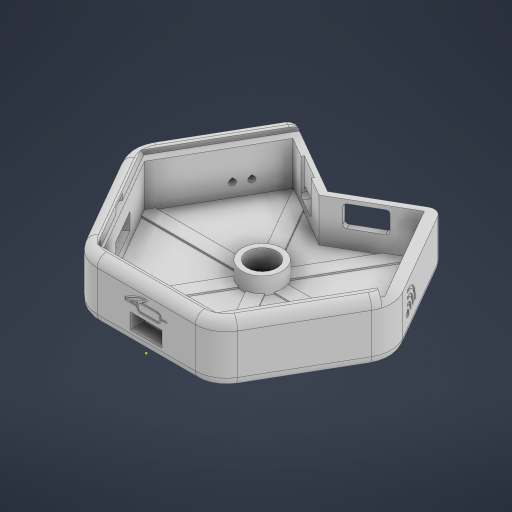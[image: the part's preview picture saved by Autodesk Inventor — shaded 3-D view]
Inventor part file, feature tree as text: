
AUTODESK INVENTOR PART (.ipt)
format: ipt  version: 2023 (Build 270158000, 158)  size: 1,028,096 bytes
history: native  units: in
note: dims shown in document units (in); Inventor stores cm internally (conversion verified against a paired STEP export)
features: extrude x21, sketch x15, move_body x9, direct_edit x6, fillet x5, draft x3, chamfer x1, other x1
ambient origin geometry x8: Origin, YZ Plane, XZ Plane, XY Plane, X Axis, Y Axis, Z Axis, Center Point
bodies: Solid1 (feature_tree)
feature tree (61):
  sketch  "Sketch1"  dims[d7=0.1772in d9=0.1772in d10=60.0deg d11=0.1772in d12=60.0deg d32=0.0787in d33=0.0in]
  extrude  "Extrusion1"  Depth=0.0787in TaperAngle=0.0deg
  extrude  "Extrusion2"  Depth=0.0984in TaperAngle=0.0deg
  extrude  "Extrusion3"  TaperAngle=0.0deg  [1 undecoded]
  extrude  "Extrusion4"  Depth=0.1575in
  direct_edit  "Direct Edit1"
  extrude  "Extrusion5"  Depth=0.1575in
  draft  "FaceDraft2"
  direct_edit  "Direct Edit2"
  direct_edit  "Direct Edit3"
  extrude  "Extrusion6"  [1 undecoded]
  draft  "FaceDraft5"
  draft  "FaceDraft6"
  direct_edit  "Direct Edit5"
  extrude  "Extrusion8"  Depth=0.0039in TaperAngle=0.0deg
  extrude  "Extrusion9"  Depth=0.1969in
  direct_edit  "Direct Edit6"
  extrude  "Extrusion10"  Depth=0.0197in
  fillet  "Fillet1"  Radius=0.0984in
  extrude  "Extrusion11"  Depth=0.0984in
  fillet  "Fillet2"  Radius=0.0984in
  extrude  "Extrusion12"  [1 undecoded]
  extrude  "Extrusion13"  TaperAngle=0.0deg  [1 undecoded]
  extrude  "Extrusion14"  Depth=0.374in
  fillet  "Fillet3"  Radius=0.5118in
  fillet  "Fillet4"  [1 undecoded]
  fillet  "Fillet5"  [1 undecoded]
  direct_edit  "Direct Edit7"
  extrude  "Extrusion15"  Depth=2.9528in
  extrude  "Extrusion16"  Depth=0.0236in
  extrude  "Extrusion17"  Depth=0.0236in
  extrude  "Extrusion18"  Depth=0.0236in
  extrude  "Extrusion19"  Depth=0.0236in
  extrude  "Extrusion20"  Depth=0.0236in
  sketch  "Sketch16"  dims[d86=0.0984in d87=0.0in d88=0.374in d89=0.5118in d90=120.0deg d91=60.0deg]
  extrude  "Extrusion22"  Depth=0.0236in
  chamfer  "Chamfer1"  Angle=60.0deg  [1 undecoded]
  extrude  "Extrusion23"  Depth=0.0236in
  sketch  "Sketch3"  dims[d34=0.6299in d35=0.0in d36=0.0984in d37=0.0in]
  sketch  "Sketch4"  dims[d38=0.2953in d39=0.0in]
  sketch  "Sketch5"  dims[d41=0.0in d42=0.0in d43=-0.0394in d44=0.1575in]
  sketch  "Sketch6"  dims[d45=0.1575in d46=0.1575in]
  sketch  "Sketch8"  dims[d47=0.1181in d48=0.0in d50=-0.2405in]
  sketch  "Sketch9"  dims[d51=0.0in d52=0.0in d53=-0.13in d54=0.0in d55=0.0in d56=0.0039in]
  sketch  "Sketch10"  dims[d57=0.0in d58=0.0in d59=0.0039in d60=0.1969in]
  sketch  "Sketch11"  dims[d61=0.0984in d62=0.0in d63=0.0197in d74=0.0984in]
  sketch  "Sketch12"  dims[d75=0.0984in d76=0.0984in d77=0.0984in]
  sketch  "Sketch13"  dims[d78=0.3436in d79=-0.3436in]
  other  "Image1"
  sketch  "Sketch14"  dims[d80=0.0in d81=0.0in d82=-0.561in d83=0.0in d84=0.0in d85=-0.561in]
  sketch  "Sketch17"  dims[d93=0.1772in d94=2.9528in]
  sketch  "Sketch18"  dims[d95=0.1772in d96=0.1772in d97=0.1772in d98=0.0886in d99=0.0886in d100=0.1772in d101=0.1772in d102=60.0deg d104=0.1772in d105=0.0886in d106=1.5748in d107=0.0315in d108=0.1772in d109=0.1772in d110=0.4488in d111=0.0in d112=0.0in d113=0.0in d114=-0.0157in d115=0.3189in d116=0.4488in d117=0.0in d118=0.0492in d119=0.3819in d120=0.0492in d121=0.2205in d122=0.2205in d123=0.2756in d124=0.4488in d125=0.0in d126=0.0394in d127=0.1181in d128=0.0492in d129=0.2362in d130=0.1378in d131=0.0in d132=0.5276in d133=0.2677in d134=0.2835in d135=0.0in d136=0.0in d137=0.2461in d138=0.1969in d139=0.0in d140=0.5433in d141=0.1516in d142=0.1969in d143=0.2008in d144=0.1969in d145=0.0in d146=0.1181in d147=0.3937in d148=0.1181in d149=0.0in d150=0.0in d151=-0.0118in d152=0.0in d153=0.0in d154=-0.0118in d155=0.2854in d156=0.3189in d157=0.0768in d158=0.3937in d159=0.0in d160=0.4134in d161=0.3425in d162=0.0768in d163=0.1811in d164=0.0768in d165=0.3937in d166=0.0in d167=0.5497in d168=0.5497in d169=0.5497in d170=0.0433in d171=0.0315in d172=0.0433in d173=0.0315in d174=0.0433in d175=0.0315in d176=0.0098in d177=0.0in d185=0.3543in d186=0.1772in d187=0.3543in d188=0.0276in d189=0.0669in d190=0.0098in d191=0.0in d192=0.0197in d214=0.0787in d219=0.0063in d224=0.1441in d227=0.0567in d228=0.0177in d229=0.0177in d236=0.0177in d237=0.0878in d238=0.0898in d242=0.0457in d243=0.0307in d245=0.872in d264=0.022in d265=0.0697in d266=0.8562in d268=0.0177in d277=0.0177in d279=0.0069in d281=0.0445in d283=0.1009in d285=0.0445in d288=0.0181in d290=0.0098in d291=0.0in d293=0.1378in d294=0.3197in d295=0.0591in d296=0.0276in d297=0.0098in d298=0.0in d301=0.0315in d302=0.0189in d303=0.2756in d305=0.0472in d316=0.0098in d317=0.0in d324=0.126in d328=0.0157in d329=0.0189in d330=0.0208in d331=0.0126in d332=0.0374in d333=0.0189in d335=0.1673in d342=0.0189in d343=0.1996in d344=0.2913in d345=0.2484in d346=0.0638in d347=0.0579in d348=0.0197in d349=0.0189in d350=0.2165in d351=0.1535in d353=0.3465in d355=0.0709in d357=0.0394in d358=0.1772in d359=45.0deg d365=0.0098in d366=0.0in d369=0.0236in d372=0.1575in d373=0.0236in d3=0.0197in d4=0.0344in d5=0.0197in d6=0.0344in d360=0.0197in d361=0.0344in d362=0.0197in d363=0.0344in]
  move_body  "Move1"
  move_body  "Move2"
  move_body  "Move3"
  move_body  "Move4"
  move_body  "Move7"
  move_body  "Move8"
  move_body  "Move9"
  move_body  "Move10"
  move_body  "Move11"
note: 7 required parameter values undecoded (feature->parameter linkage not recoverable at this tier; creation-order binding heuristic only, values carry confidence <= 0.55)
